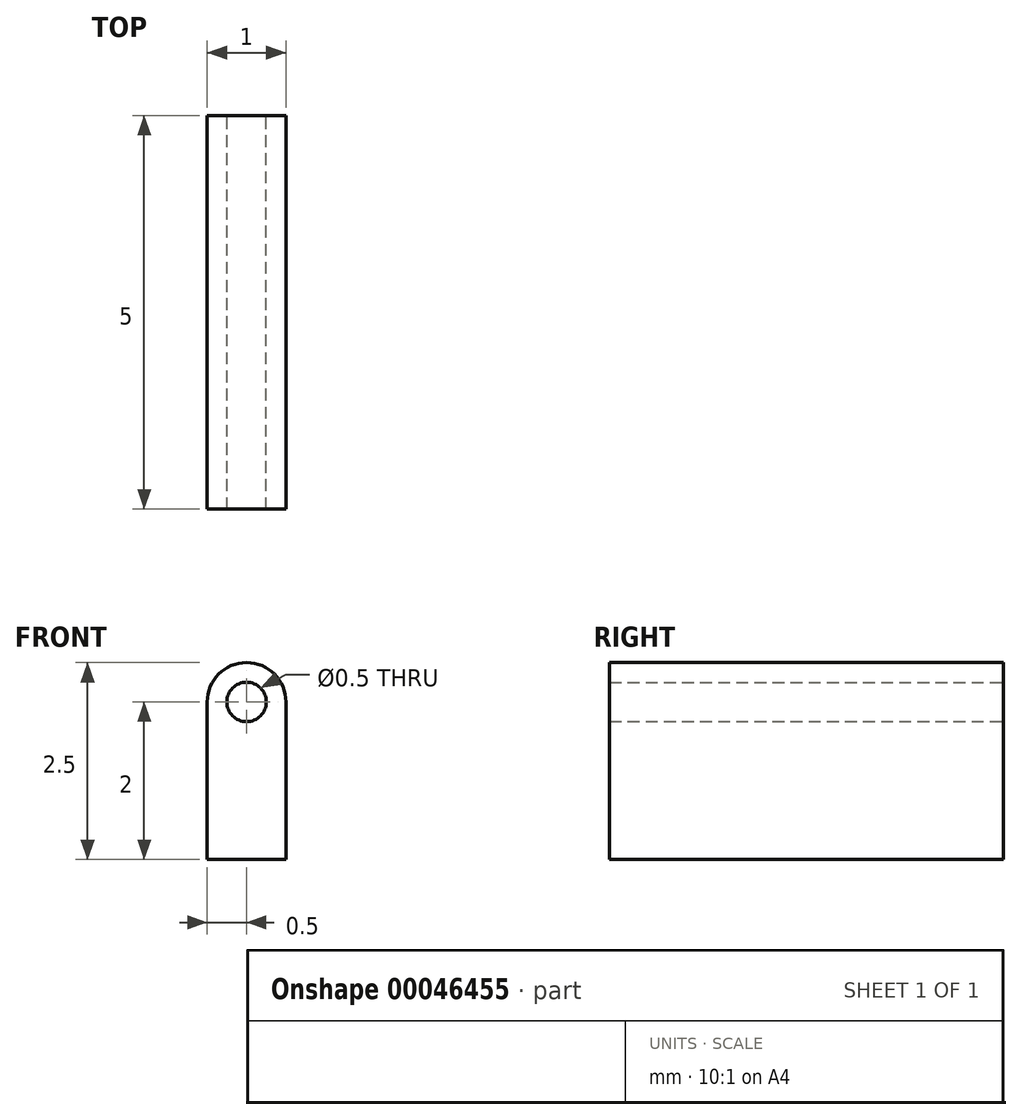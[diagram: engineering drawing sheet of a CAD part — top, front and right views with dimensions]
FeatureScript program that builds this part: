
annotation { "Feature Type Name" : "Feature", "Feature Type Description" : "" }
export const myFeature = defineFeature(function(context is Context, id is Id, definition is map)
    precondition{}
    {
        {
            var Q0;
            Q0=qCreatedBy(makeId("Front.planeOp"),FACE);
            var sketch = newSketch(context, id + "F0", { "sketchPlane" : qUnion([Q0])});
            skCircle(sketch, "E0", {"center": v(0, 0) * mm, "radius": 0.25 * mm});
            skArc(sketch, "E1", {"start": v(-0.5, 0) * mm, "mid": v(0, 0.5) * mm, "end": v(0.5, 0) * mm});
            skLineSegment(sketch, "E2", {"start": v(-0.5, 0) * mm, "end": v(-0.5, -2) * mm});
            skLineSegment(sketch, "E3", {"start": v(-0.5, -2) * mm, "end": v(0.5, -2) * mm});
            skLineSegment(sketch, "E4", {"start": v(0.5, -2) * mm, "end": v(0.5, 0) * mm});
            skSolve(sketch);
        }
        {
            var Q0;
            Q0=makeQuery(id+"F0.imprint","IMPRINT",FACE,{"disambiguationData":[TD([[makeQuery(id+"F0.imprint","IMPRINT",EDGE,{"derivedFrom":sQuery(id+"F0.wireOp",EDGE,"E0")}),-1.0]])]});
            extrude(context, id + "F1", {"entities" : qUnion([Q0]), "depth" : 5 * mm});
        }
    });
